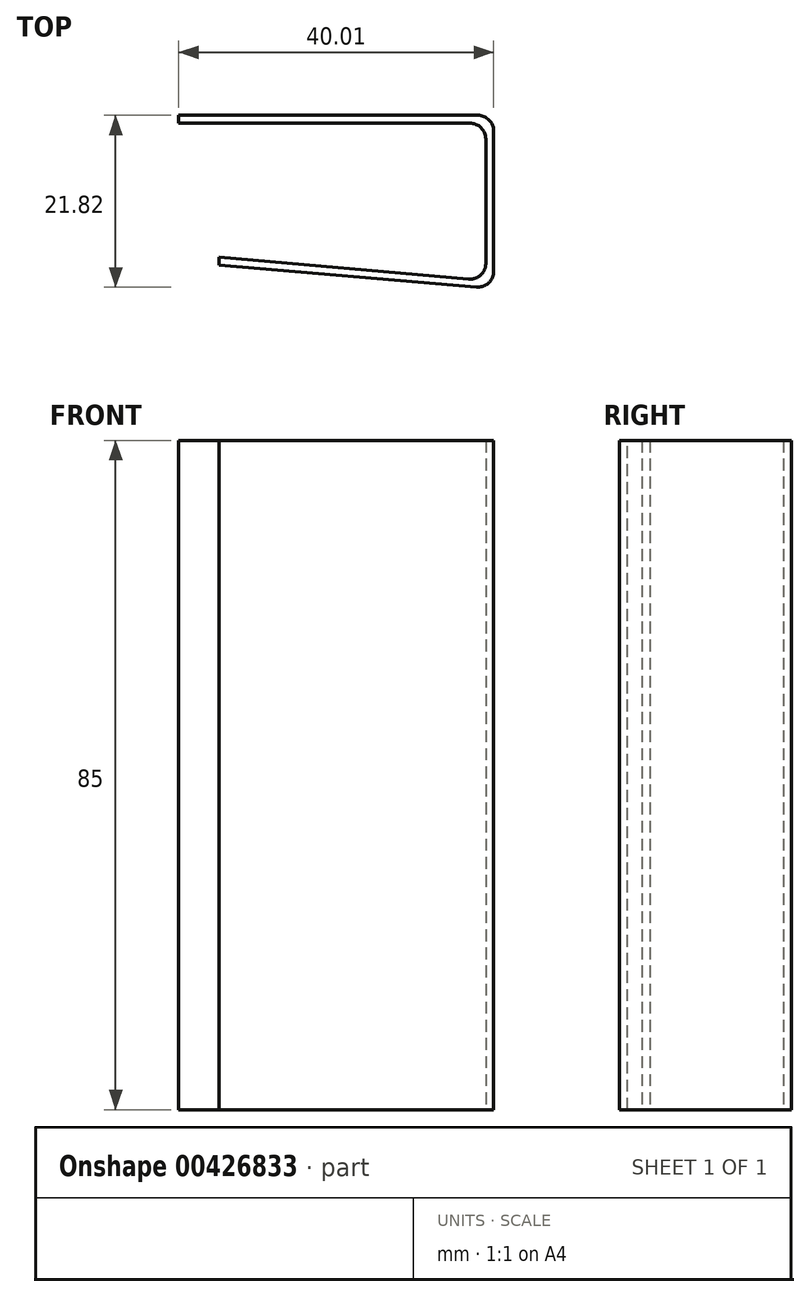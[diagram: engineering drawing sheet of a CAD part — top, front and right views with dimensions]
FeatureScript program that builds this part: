
annotation { "Feature Type Name" : "Feature", "Feature Type Description" : "" }
export const myFeature = defineFeature(function(context is Context, id is Id, definition is map)
    precondition{}
    {
        {
            var Q0;
            Q0=qCreatedBy(makeId("Top.planeOp"),FACE);
            var sketch = newSketch(context, id + "F0", { "sketchPlane" : qUnion([Q0])});
            skLineSegment(sketch, "E0", {"start": v(-37.2, 11.65) * mm, "end": v(2.8, 11.65) * mm});
            skLineSegment(sketch, "E1", {"start": v(2.8, 11.65) * mm, "end": v(2.8, -10.35) * mm});
            skLineSegment(sketch, "E2", {"start": v(1.8, -9.35) * mm, "end": v(1.8, 10.65) * mm});
            skLineSegment(sketch, "E3", {"start": v(1.8, 10.65) * mm, "end": v(-37.2, 10.65) * mm});
            skLineSegment(sketch, "E4", {"start": v(-37.2, 10.65) * mm, "end": v(-37.2, 11.65) * mm});
            skLineSegment(sketch, "E5", {"start": v(-32.08, -7.35) * mm, "end": v(-32.08, -6.35) * mm});
            skLineSegment(sketch, "E6", {"start": v(-32.08, -7.35) * mm, "end": v(2.8, -10.35) * mm});
            skLineSegment(sketch, "E7", {"start": v(-32.08, -6.35) * mm, "end": v(1.8, -9.35) * mm});
            skSolve(sketch);
        }
        {
            var Q0;
            Q0=makeQuery(id+"F0.imprint","IMPRINT",FACE,{"disambiguationData":[TD([[makeQuery(id+"F0.imprint","IMPRINT",EDGE,{"derivedFrom":sQuery(id+"F0.wireOp",EDGE,"E0")}),-1.0]])]});
            extrude(context, id + "F1", {"entities" : qUnion([Q0]), "depth" : 85 * mm});
        }
        {
            var Q0;
            Q0=makeQuery(id+"F1.opExtrude","SWEPT_EDGE",EDGE,{"disambiguationData":[OSD([sQuery(id+"F0.wireOp",EDGE,"E1"),sQuery(id+"F0.wireOp",EDGE,"E6")])]});
            var Q1;
            Q1=makeQuery(id+"F1.opExtrude","SWEPT_EDGE",EDGE,{"disambiguationData":[OSD([sQuery(id+"F0.wireOp",EDGE,"E0"),sQuery(id+"F0.wireOp",EDGE,"E1")])]});
            var Q2;
            Q2=makeQuery(id+"F1.opExtrude","SWEPT_EDGE",EDGE,{"disambiguationData":[OSD([sQuery(id+"F0.wireOp",EDGE,"E2"),sQuery(id+"F0.wireOp",EDGE,"E7")])]});
            var Q3;
            Q3=makeQuery(id+"F1.opExtrude","SWEPT_EDGE",EDGE,{"disambiguationData":[OSD([sQuery(id+"F0.wireOp",EDGE,"E2"),sQuery(id+"F0.wireOp",EDGE,"E3")])]});
            fillet(context, id + "F2", {"entities" : qUnion([Q0, Q1, Q2, Q3]), "radius" : 2 * mm, "tangentPropagation" : true, "allowEdgeOverflow" : false});
        }
    });
